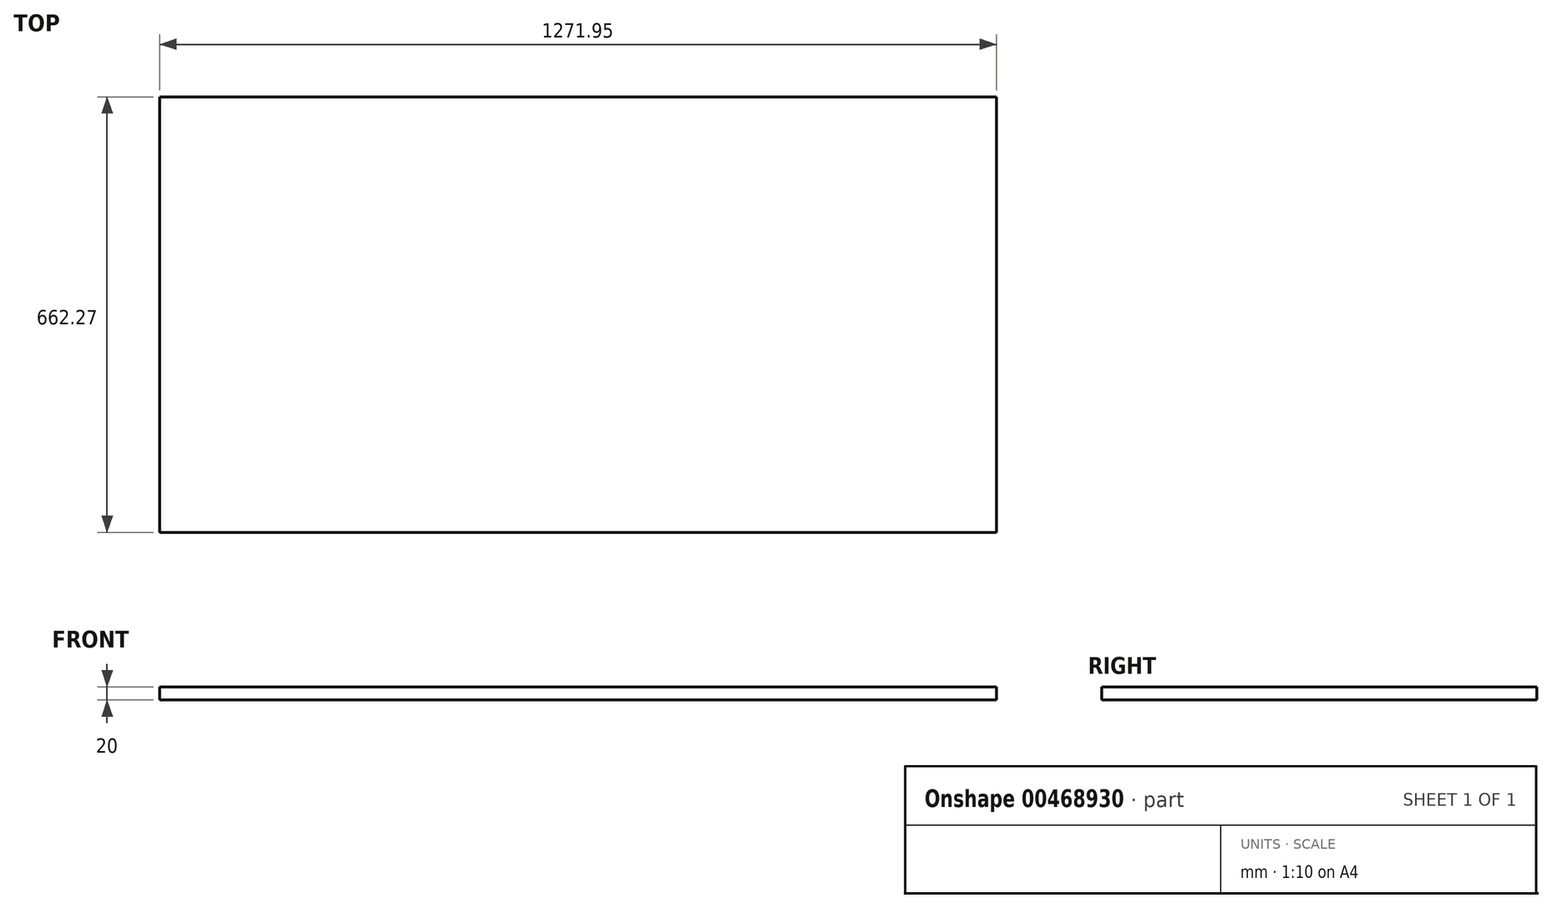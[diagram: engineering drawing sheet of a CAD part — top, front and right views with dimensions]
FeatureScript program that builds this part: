
annotation { "Feature Type Name" : "Feature", "Feature Type Description" : "" }
export const myFeature = defineFeature(function(context is Context, id is Id, definition is map)
    precondition{}
    {
        {
            var Q0;
            Q0=qCreatedBy(makeId("Top.planeOp"),FACE);
            var sketch = newSketch(context, id + "F0", { "sketchPlane" : qUnion([Q0])});
            skLineSegment(sketch, "E0.bottom", {"start": v(-783.2, 510.92) * mm, "end": v(488.76, 510.92) * mm});
            skLineSegment(sketch, "E0.top", {"start": v(-783.2, -151.35) * mm, "end": v(488.76, -151.35) * mm});
            skLineSegment(sketch, "E0.left", {"start": v(-783.2, 510.92) * mm, "end": v(-783.2, -151.35) * mm});
            skLineSegment(sketch, "E0.right", {"start": v(488.76, 510.92) * mm, "end": v(488.76, -151.35) * mm});
            skSolve(sketch);
        }
        {
            var Q0;
            Q0 = qSketchRegion(id + "F0", true);
            var Q1;
            Q1=sQuery(id+"F0.wireOp",EDGE,"E0.top");
            var Q2;
            Q2=sQuery(id+"F0.wireOp",EDGE,"E0.right");
            extrude(context, id + "F1", {"bodyType" : ToolBodyType.SURFACE, "surfaceEntities" : qUnion([Q0, Q1, Q2]), "depth" : 20 * mm});
        }
    });
